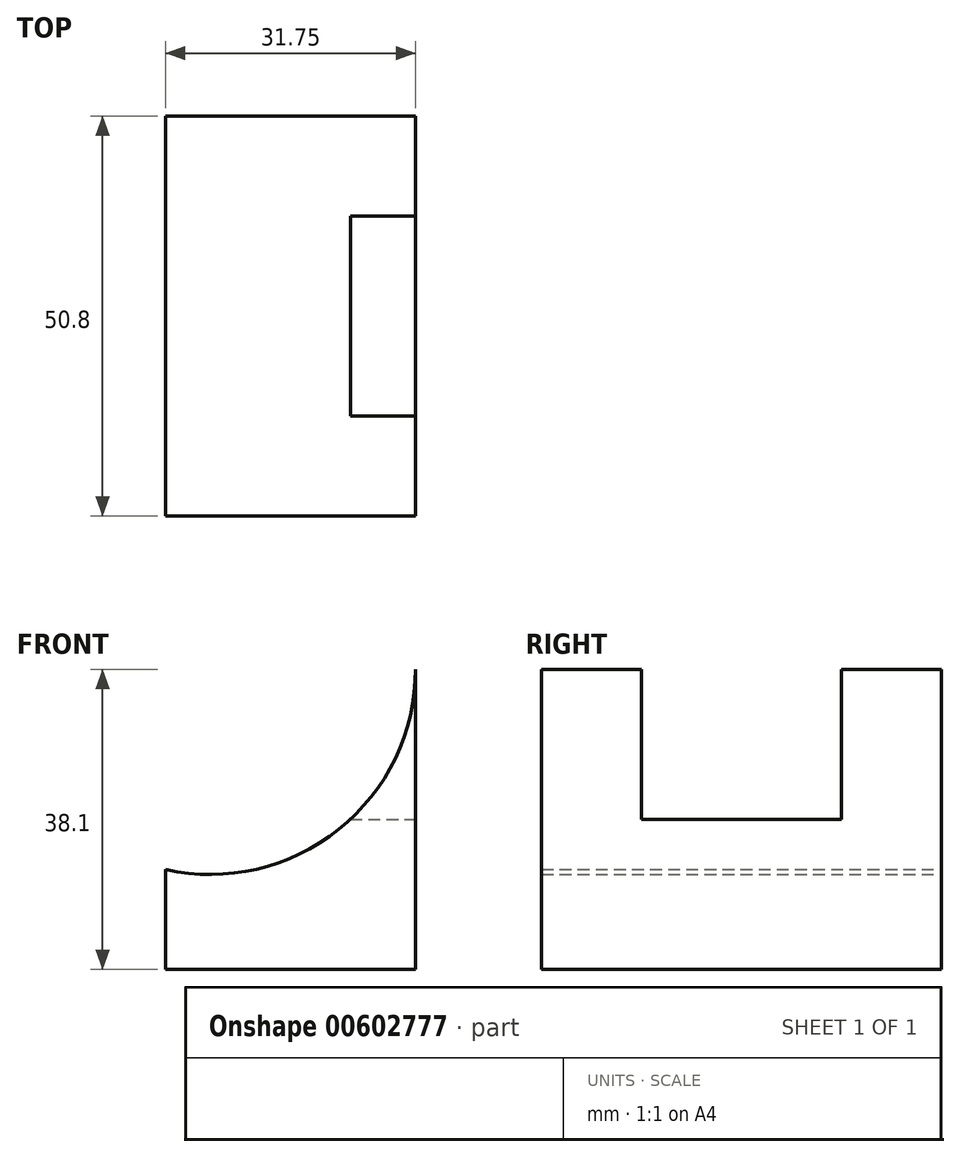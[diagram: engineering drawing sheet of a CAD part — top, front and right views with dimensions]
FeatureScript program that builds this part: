
annotation { "Feature Type Name" : "Feature", "Feature Type Description" : "" }
export const myFeature = defineFeature(function(context is Context, id is Id, definition is map)
    precondition{}
    {
        {
            var Q0;
            Q0=qCreatedBy(makeId("Front.planeOp"),FACE);
            var sketch = newSketch(context, id + "F0", { "sketchPlane" : qUnion([Q0])});
            skLineSegment(sketch, "E0", {"start": v(0, 0) * mm, "end": v(31.75, 0) * mm});
            skLineSegment(sketch, "E1", {"start": v(31.75, 0) * mm, "end": v(31.75, 38.1) * mm});
            skLineSegment(sketch, "E2", {"start": v(0, 0) * mm, "end": v(0, 12.7) * mm});
            skArc(sketch, "E3", {"start": v(0, 12.7) * mm, "mid": v(21.98, 17.77) * mm, "end": v(31.75, 38.1) * mm});
            skSolve(sketch);
        }
        {
            var Q0;
            Q0=makeQuery(id+"F0.imprint","IMPRINT",FACE,{"disambiguationData":[TD([[makeQuery(id+"F0.imprint","IMPRINT",EDGE,{"derivedFrom":sQuery(id+"F0.wireOp",EDGE,"E0")}),1.0]])]});
            extrude(context, id + "F1", {"entities" : qUnion([Q0]), "depth" : 50.8 * mm, "offsetDistance" : 25.4 * mm});
        }
        {
            var Q0;
            Q0=makeQuery(id+"F1.opExtrude","SWEPT_FACE",FACE,{"disambiguationData":[OSD([sQuery(id+"F0.wireOp",EDGE,"E1")])]});
            var sketch = newSketch(context, id + "F2", { "sketchPlane" : qUnion([Q0])});
            skLineSegment(sketch, "E4", {"start": v(-50.8, 38.1) * mm, "end": v(-38.1, 38.1) * mm});
            skLineSegment(sketch, "E5", {"start": v(-38.1, 38.1) * mm, "end": v(-38.1, 19.05) * mm});
            skLineSegment(sketch, "E6", {"start": v(-38.1, 19.05) * mm, "end": v(-12.7, 19.05) * mm});
            skLineSegment(sketch, "E7", {"start": v(-12.7, 19.05) * mm, "end": v(-12.7, 38.1) * mm});
            skLineSegment(sketch, "E8", {"start": v(-12.7, 38.1) * mm, "end": v(0, 38.1) * mm});
            skSolve(sketch);
        }
        {
            var Q0;
            {var subQ0=sQuery(id+"F2.wireOp",EDGE,"E5");Q0=makeQuery(id+"F2.imprint","IMPRINT",FACE,{"disambiguationData":[TD([[makeQuery(id+"F2.imprint","IMPRINT",EDGE,{"derivedFrom":subQ0}),1.0]])]});}
            extrude(context, id + "F3", {"entities" : qUnion([Q0]), "operationType" : NewBodyOperationType.REMOVE, "oppositeDirection" : true, "depth" : 25.4 * mm, "offsetDistance" : 25.4 * mm});
        }
    });
